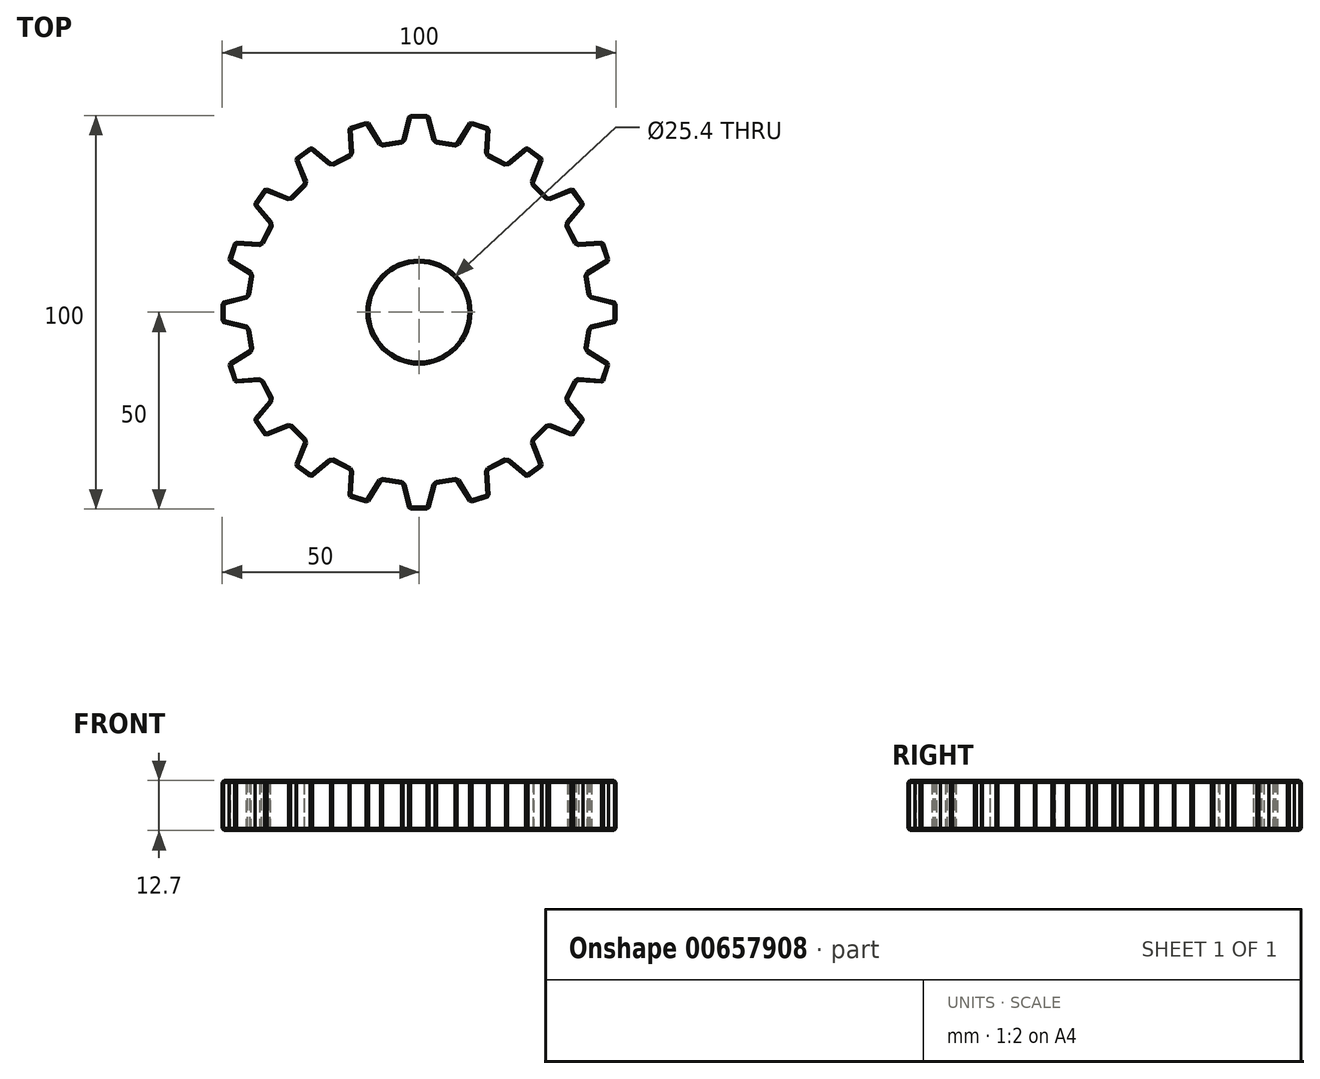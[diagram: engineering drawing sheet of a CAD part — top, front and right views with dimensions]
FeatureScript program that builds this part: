
annotation { "Feature Type Name" : "Feature", "Feature Type Description" : "" }
export const myFeature = defineFeature(function(context is Context, id is Id, definition is map)
    precondition{}
    {
        {
            var Q0;
            Q0=qCreatedBy(makeId("Top.planeOp"),FACE);
            var sketch = newSketch(context, id + "F0", { "sketchPlane" : qUnion([Q0])});
            skLineSegment(sketch, "E0", {"start": v(2.5, 50) * mm, "end": v(4.11, 43.54) * mm});
            skLineSegment(sketch, "E1.MirrorCS", {"start": v(-2.5, 50) * mm, "end": v(-4.11, 43.54) * mm});
            skLineSegment(sketch, "E2", {"start": v(4.11, 43.54) * mm, "end": v(9.54, 42.68) * mm});
            skLineSegment(sketch, "E3", {"start": v(-2.5, 50) * mm, "end": v(2.5, 50) * mm});
            skLineSegment(sketch, "E4", {"start": v(6.83, 43.1) * mm, "end": v(7.6, 48.05) * mm, "construction": true});
            skLineSegment(sketch, "E5.1.0", {"start": v(-17.83, 46.78) * mm, "end": v(-17.36, 40.14) * mm});
            skLineSegment(sketch, "E5.1.1", {"start": v(-17.83, 46.78) * mm, "end": v(-13.07, 48.33) * mm});
            skLineSegment(sketch, "E5.1.2", {"start": v(-13.07, 48.33) * mm, "end": v(-9.54, 42.68) * mm});
            skLineSegment(sketch, "E5.1.3", {"start": v(-9.54, 42.68) * mm, "end": v(-4.11, 43.54) * mm});
            skLineSegment(sketch, "E5.2.0", {"start": v(-31.41, 38.98) * mm, "end": v(-28.92, 32.8) * mm});
            skLineSegment(sketch, "E5.2.1", {"start": v(-31.41, 38.98) * mm, "end": v(-27.37, 41.92) * mm});
            skLineSegment(sketch, "E5.2.2", {"start": v(-27.37, 41.92) * mm, "end": v(-22.26, 37.64) * mm});
            skLineSegment(sketch, "E5.2.3", {"start": v(-22.26, 37.64) * mm, "end": v(-17.36, 40.14) * mm});
            skPoint(sketch, "E5.center", {"position": v(0, 0) * mm});
            skLineSegment(sketch, "E6.2.3.0", {"start": v(-41.92, 27.37) * mm, "end": v(-37.64, 22.26) * mm});
            skLineSegment(sketch, "E6.3.3.0", {"start": v(-41.92, 27.37) * mm, "end": v(-38.98, 31.41) * mm});
            skLineSegment(sketch, "E6.6.3.0", {"start": v(-38.98, 31.41) * mm, "end": v(-32.8, 28.92) * mm});
            skLineSegment(sketch, "E6.9.3.0", {"start": v(-32.8, 28.92) * mm, "end": v(-28.92, 32.8) * mm});
            skLineSegment(sketch, "E6.2.4.0", {"start": v(-48.33, 13.07) * mm, "end": v(-42.68, 9.54) * mm});
            skLineSegment(sketch, "E6.3.4.0", {"start": v(-48.33, 13.07) * mm, "end": v(-46.78, 17.83) * mm});
            skLineSegment(sketch, "E6.6.4.0", {"start": v(-46.78, 17.83) * mm, "end": v(-40.14, 17.36) * mm});
            skLineSegment(sketch, "E6.9.4.0", {"start": v(-40.14, 17.36) * mm, "end": v(-37.64, 22.26) * mm});
            skLineSegment(sketch, "E6.2.5.0", {"start": v(-50, -2.5) * mm, "end": v(-43.54, -4.11) * mm});
            skLineSegment(sketch, "E6.3.5.0", {"start": v(-50, -2.5) * mm, "end": v(-50, 2.5) * mm});
            skLineSegment(sketch, "E6.6.5.0", {"start": v(-50, 2.5) * mm, "end": v(-43.54, 4.11) * mm});
            skLineSegment(sketch, "E6.9.5.0", {"start": v(-43.54, 4.11) * mm, "end": v(-42.68, 9.54) * mm});
            skLineSegment(sketch, "E6.2.6.0", {"start": v(-46.78, -17.83) * mm, "end": v(-40.14, -17.36) * mm});
            skLineSegment(sketch, "E6.3.6.0", {"start": v(-46.78, -17.83) * mm, "end": v(-48.33, -13.07) * mm});
            skLineSegment(sketch, "E6.6.6.0", {"start": v(-48.33, -13.07) * mm, "end": v(-42.68, -9.54) * mm});
            skLineSegment(sketch, "E6.9.6.0", {"start": v(-42.68, -9.54) * mm, "end": v(-43.54, -4.11) * mm});
            skLineSegment(sketch, "E6.2.7.0", {"start": v(-38.98, -31.41) * mm, "end": v(-32.8, -28.92) * mm});
            skLineSegment(sketch, "E6.3.7.0", {"start": v(-38.98, -31.41) * mm, "end": v(-41.92, -27.37) * mm});
            skLineSegment(sketch, "E6.6.7.0", {"start": v(-41.92, -27.37) * mm, "end": v(-37.64, -22.26) * mm});
            skLineSegment(sketch, "E6.9.7.0", {"start": v(-37.64, -22.26) * mm, "end": v(-40.14, -17.36) * mm});
            skLineSegment(sketch, "E6.2.8.0", {"start": v(-27.37, -41.92) * mm, "end": v(-22.26, -37.64) * mm});
            skLineSegment(sketch, "E6.3.8.0", {"start": v(-27.37, -41.92) * mm, "end": v(-31.41, -38.98) * mm});
            skLineSegment(sketch, "E6.6.8.0", {"start": v(-31.41, -38.98) * mm, "end": v(-28.92, -32.8) * mm});
            skLineSegment(sketch, "E6.9.8.0", {"start": v(-28.92, -32.8) * mm, "end": v(-32.8, -28.92) * mm});
            skLineSegment(sketch, "E6.2.9.0", {"start": v(-13.07, -48.33) * mm, "end": v(-9.54, -42.68) * mm});
            skLineSegment(sketch, "E6.3.9.0", {"start": v(-13.07, -48.33) * mm, "end": v(-17.83, -46.78) * mm});
            skLineSegment(sketch, "E6.6.9.0", {"start": v(-17.83, -46.78) * mm, "end": v(-17.36, -40.14) * mm});
            skLineSegment(sketch, "E6.9.9.0", {"start": v(-17.36, -40.14) * mm, "end": v(-22.26, -37.64) * mm});
            skLineSegment(sketch, "E6.2.10.0", {"start": v(2.5, -50) * mm, "end": v(4.11, -43.54) * mm});
            skLineSegment(sketch, "E6.3.10.0", {"start": v(2.5, -50) * mm, "end": v(-2.5, -50) * mm});
            skLineSegment(sketch, "E6.6.10.0", {"start": v(-2.5, -50) * mm, "end": v(-4.11, -43.54) * mm});
            skLineSegment(sketch, "E6.9.10.0", {"start": v(-4.11, -43.54) * mm, "end": v(-9.54, -42.68) * mm});
            skLineSegment(sketch, "E6.2.11.0", {"start": v(17.83, -46.78) * mm, "end": v(17.36, -40.14) * mm});
            skLineSegment(sketch, "E6.3.11.0", {"start": v(17.83, -46.78) * mm, "end": v(13.07, -48.33) * mm});
            skLineSegment(sketch, "E6.6.11.0", {"start": v(13.07, -48.33) * mm, "end": v(9.54, -42.68) * mm});
            skLineSegment(sketch, "E6.9.11.0", {"start": v(9.54, -42.68) * mm, "end": v(4.11, -43.54) * mm});
            skLineSegment(sketch, "E6.2.12.0", {"start": v(31.41, -38.98) * mm, "end": v(28.92, -32.8) * mm});
            skLineSegment(sketch, "E6.3.12.0", {"start": v(31.41, -38.98) * mm, "end": v(27.37, -41.92) * mm});
            skLineSegment(sketch, "E6.6.12.0", {"start": v(27.37, -41.92) * mm, "end": v(22.26, -37.64) * mm});
            skLineSegment(sketch, "E6.9.12.0", {"start": v(22.26, -37.64) * mm, "end": v(17.36, -40.14) * mm});
            skLineSegment(sketch, "E6.2.13.0", {"start": v(41.92, -27.37) * mm, "end": v(37.64, -22.26) * mm});
            skLineSegment(sketch, "E6.3.13.0", {"start": v(41.92, -27.37) * mm, "end": v(38.98, -31.41) * mm});
            skLineSegment(sketch, "E6.6.13.0", {"start": v(38.98, -31.41) * mm, "end": v(32.8, -28.92) * mm});
            skLineSegment(sketch, "E6.9.13.0", {"start": v(32.8, -28.92) * mm, "end": v(28.92, -32.8) * mm});
            skLineSegment(sketch, "E6.2.14.0", {"start": v(48.33, -13.07) * mm, "end": v(42.68, -9.54) * mm});
            skLineSegment(sketch, "E6.3.14.0", {"start": v(48.33, -13.07) * mm, "end": v(46.78, -17.83) * mm});
            skLineSegment(sketch, "E6.6.14.0", {"start": v(46.78, -17.83) * mm, "end": v(40.14, -17.36) * mm});
            skLineSegment(sketch, "E6.9.14.0", {"start": v(40.14, -17.36) * mm, "end": v(37.64, -22.26) * mm});
            skLineSegment(sketch, "E6.2.15.0", {"start": v(50, 2.5) * mm, "end": v(43.54, 4.11) * mm});
            skLineSegment(sketch, "E6.3.15.0", {"start": v(50, 2.5) * mm, "end": v(50, -2.5) * mm});
            skLineSegment(sketch, "E6.6.15.0", {"start": v(50, -2.5) * mm, "end": v(43.54, -4.11) * mm});
            skLineSegment(sketch, "E6.9.15.0", {"start": v(43.54, -4.11) * mm, "end": v(42.68, -9.54) * mm});
            skLineSegment(sketch, "E6.2.16.0", {"start": v(46.78, 17.83) * mm, "end": v(40.14, 17.36) * mm});
            skLineSegment(sketch, "E6.3.16.0", {"start": v(46.78, 17.83) * mm, "end": v(48.33, 13.07) * mm});
            skLineSegment(sketch, "E6.6.16.0", {"start": v(48.33, 13.07) * mm, "end": v(42.68, 9.54) * mm});
            skLineSegment(sketch, "E6.9.16.0", {"start": v(42.68, 9.54) * mm, "end": v(43.54, 4.11) * mm});
            skLineSegment(sketch, "E6.2.17.0", {"start": v(38.98, 31.41) * mm, "end": v(32.8, 28.92) * mm});
            skLineSegment(sketch, "E6.3.17.0", {"start": v(38.98, 31.41) * mm, "end": v(41.92, 27.37) * mm});
            skLineSegment(sketch, "E6.6.17.0", {"start": v(41.92, 27.37) * mm, "end": v(37.64, 22.26) * mm});
            skLineSegment(sketch, "E6.9.17.0", {"start": v(37.64, 22.26) * mm, "end": v(40.14, 17.36) * mm});
            skLineSegment(sketch, "E6.2.18.0", {"start": v(27.37, 41.92) * mm, "end": v(22.26, 37.64) * mm});
            skLineSegment(sketch, "E6.3.18.0", {"start": v(27.37, 41.92) * mm, "end": v(31.41, 38.98) * mm});
            skLineSegment(sketch, "E6.6.18.0", {"start": v(31.41, 38.98) * mm, "end": v(28.92, 32.8) * mm});
            skLineSegment(sketch, "E6.9.18.0", {"start": v(28.92, 32.8) * mm, "end": v(32.8, 28.92) * mm});
            skLineSegment(sketch, "E6.2.19.0", {"start": v(13.07, 48.33) * mm, "end": v(9.54, 42.68) * mm});
            skLineSegment(sketch, "E6.3.19.0", {"start": v(13.07, 48.33) * mm, "end": v(17.83, 46.78) * mm});
            skLineSegment(sketch, "E6.6.19.0", {"start": v(17.83, 46.78) * mm, "end": v(17.36, 40.14) * mm});
            skLineSegment(sketch, "E6.9.19.0", {"start": v(17.36, 40.14) * mm, "end": v(22.26, 37.64) * mm});
            skLineSegment(sketch, "E7", {"start": v(0, 50) * mm, "end": v(0, 0) * mm, "construction": true});
            skLineSegment(sketch, "E8", {"start": v(-4.11, 43.54) * mm, "end": v(4.11, 43.54) * mm, "construction": true});
            skCircle(sketch, "E9", {"center": v(0, 0) * mm, "radius": 12.7 * mm});
            skSolve(sketch);
        }
        {
            var Q0;
            Q0=makeQuery(id+"F0.imprint","IMPRINT",FACE,{"disambiguationData":[TD([[makeQuery(id+"F0.imprint","IMPRINT",EDGE,{"derivedFrom":sQuery(id+"F0.wireOp",EDGE,"E0")}),-1.0]])]});
            var Q1;
            Q1=sQuery(id+"F0.wireOp",EDGE,"E6.3.6.0");
            var Q2;
            Q2=sQuery(id+"F0.wireOp",EDGE,"E6.9.6.0");
            var Q3;
            Q3=sQuery(id+"F0.wireOp",EDGE,"E6.2.5.0");
            var Q4;
            Q4=sQuery(id+"F0.wireOp",EDGE,"E6.3.5.0");
            var Q5;
            Q5=sQuery(id+"F0.wireOp",EDGE,"E6.6.5.0");
            var Q6;
            Q6=sQuery(id+"F0.wireOp",EDGE,"E6.9.5.0");
            var Q7;
            Q7=sQuery(id+"F0.wireOp",EDGE,"E6.2.4.0");
            var Q8;
            Q8=sQuery(id+"F0.wireOp",EDGE,"E6.3.4.0");
            var Q9;
            Q9=sQuery(id+"F0.wireOp",EDGE,"E6.6.4.0");
            var Q10;
            Q10=sQuery(id+"F0.wireOp",EDGE,"E6.9.4.0");
            var Q11;
            Q11=sQuery(id+"F0.wireOp",EDGE,"E6.2.3.0");
            var Q12;
            Q12=sQuery(id+"F0.wireOp",EDGE,"E6.3.3.0");
            var Q13;
            Q13=sQuery(id+"F0.wireOp",EDGE,"E6.6.3.0");
            var Q14;
            Q14=sQuery(id+"F0.wireOp",EDGE,"E5.2.0");
            var Q15;
            Q15=sQuery(id+"F0.wireOp",EDGE,"E6.9.3.0");
            var Q16;
            Q16=sQuery(id+"F0.wireOp",EDGE,"E6.6.6.0");
            extrude(context, id + "F1", {"entities" : qUnion([Q0]), "surfaceEntities" : qUnion([Q1, Q2, Q3, Q4, Q5, Q6, Q7, Q8, Q9, Q10, Q11, Q12, Q13, Q14, Q15, Q16]), "endBound" : BoundingType.SYMMETRIC, "depth" : 12.7 * mm, "offsetDistance" : 25 * mm, "hasSecondDirectionDraft" : true, "secondDirectionDraftAngle" : 5 * degree});
        }
        {
            var Q0;
            Q0=makeQuery(id+"F1.opExtrude","SWEPT_FACE",FACE,{"disambiguationData":[OSD([sQuery(id+"F0.wireOp",EDGE,"E5.2.0")])]});
            var Q1;
            Q1=makeQuery(id+"F1.opExtrude","CAP_EDGE",EDGE,{"disambiguationData":[OSD([sQuery(id+"F0.wireOp",EDGE,"E6.3.17.0")])],"isStart":true});
            var Q2;
            Q2=makeQuery(id+"F1.opExtrude","CAP_EDGE",EDGE,{"disambiguationData":[OSD([sQuery(id+"F0.wireOp",EDGE,"E6.6.11.0")])],"isStart":true});
            var Q3;
            Q3=makeQuery(id+"F1.opExtrude","CAP_EDGE",EDGE,{"disambiguationData":[OSD([sQuery(id+"F0.wireOp",EDGE,"E9")])],"isStart":false});
            var Q4;
            Q4=makeQuery(id+"F1.opExtrude","SWEPT_FACE",FACE,{"disambiguationData":[OSD([sQuery(id+"F0.wireOp",EDGE,"E6.2.17.0")])]});
            var Q5;
            Q5=makeQuery(id+"F1.opExtrude","SWEPT_FACE",FACE,{"disambiguationData":[OSD([sQuery(id+"F0.wireOp",EDGE,"E6.9.12.0")])]});
            var Q6;
            Q6=makeQuery(id+"F1.opExtrude","SWEPT_FACE",FACE,{"disambiguationData":[OSD([sQuery(id+"F0.wireOp",EDGE,"E6.6.13.0")])]});
            var Q7;
            Q7=makeQuery(id+"F1.opExtrude","CAP_EDGE",EDGE,{"disambiguationData":[OSD([sQuery(id+"F0.wireOp",EDGE,"E6.6.10.0")])],"isStart":true});
            var Q8;
            Q8=makeQuery(id+"F1.opExtrude","SWEPT_EDGE",EDGE,{"disambiguationData":[OSD([sQuery(id+"F0.wireOp",EDGE,"E6.6.5.0"),sQuery(id+"F0.wireOp",EDGE,"E6.9.5.0")])]});
            var Q9;
            Q9=makeQuery(id+"F1.opExtrude","SWEPT_FACE",FACE,{"disambiguationData":[OSD([sQuery(id+"F0.wireOp",EDGE,"E6.6.8.0")])]});
            var Q10;
            Q10=makeQuery(id+"F1.opExtrude","SWEPT_FACE",FACE,{"disambiguationData":[OSD([sQuery(id+"F0.wireOp",EDGE,"E6.6.5.0")])]});
            var Q11;
            Q11=makeQuery(id+"F1.opExtrude","SWEPT_FACE",FACE,{"disambiguationData":[OSD([sQuery(id+"F0.wireOp",EDGE,"E5.2.1")])]});
            var Q12;
            Q12=makeQuery(id+"F1.opExtrude","SWEPT_FACE",FACE,{"disambiguationData":[OSD([sQuery(id+"F0.wireOp",EDGE,"E6.9.6.0")])]});
            var Q13;
            Q13=makeQuery(id+"F1.opExtrude","SWEPT_FACE",FACE,{"disambiguationData":[OSD([sQuery(id+"F0.wireOp",EDGE,"E6.6.17.0")])]});
            var Q14;
            Q14=makeQuery(id+"F1.opExtrude","CAP_EDGE",EDGE,{"disambiguationData":[OSD([sQuery(id+"F0.wireOp",EDGE,"E6.3.7.0")])],"isStart":false});
            var Q15;
            Q15=makeQuery(id+"F1.opExtrude","CAP_EDGE",EDGE,{"disambiguationData":[OSD([sQuery(id+"F0.wireOp",EDGE,"E6.2.12.0")])],"isStart":false});
            var Q16;
            Q16=makeQuery(id+"F1.opExtrude","CAP_EDGE",EDGE,{"disambiguationData":[OSD([sQuery(id+"F0.wireOp",EDGE,"E6.9.5.0")])],"isStart":true});
            var Q17;
            Q17=makeQuery(id+"F1.opExtrude","SWEPT_FACE",FACE,{"disambiguationData":[OSD([sQuery(id+"F0.wireOp",EDGE,"E6.6.11.0")])]});
            var Q18;
            Q18=makeQuery(id+"F1.opExtrude","SWEPT_FACE",FACE,{"disambiguationData":[OSD([sQuery(id+"F0.wireOp",EDGE,"E6.6.16.0")])]});
            var Q19;
            Q19=makeQuery(id+"F1.opExtrude","SWEPT_FACE",FACE,{"disambiguationData":[OSD([sQuery(id+"F0.wireOp",EDGE,"E6.3.16.0")])]});
            var Q20;
            Q20=makeQuery(id+"F1.opExtrude","CAP_EDGE",EDGE,{"disambiguationData":[OSD([sQuery(id+"F0.wireOp",EDGE,"E6.9.7.0")])],"isStart":true});
            var Q21;
            Q21=makeQuery(id+"F1.opExtrude","SWEPT_EDGE",EDGE,{"disambiguationData":[OSD([sQuery(id+"F0.wireOp",EDGE,"E6.6.12.0"),sQuery(id+"F0.wireOp",EDGE,"E6.9.12.0")])]});
            var Q22;
            Q22=makeQuery(id+"F1.opExtrude","SWEPT_EDGE",EDGE,{"disambiguationData":[OSD([sQuery(id+"F0.wireOp",EDGE,"E6.2.7.0"),sQuery(id+"F0.wireOp",EDGE,"E6.9.8.0")])]});
            var Q23;
            Q23=makeQuery(id+"F1.opExtrude","CAP_EDGE",EDGE,{"disambiguationData":[OSD([sQuery(id+"F0.wireOp",EDGE,"E6.9.9.0")])],"isStart":true});
            var Q24;
            Q24=makeQuery(id+"F1.opExtrude","SWEPT_FACE",FACE,{"disambiguationData":[OSD([sQuery(id+"F0.wireOp",EDGE,"E6.3.10.0")])]});
            var Q25;
            Q25=makeQuery(id+"F1.opExtrude","SWEPT_FACE",FACE,{"disambiguationData":[OSD([sQuery(id+"F0.wireOp",EDGE,"E6.3.4.0")])]});
            var Q26;
            Q26=makeQuery(id+"F1.opExtrude","SWEPT_FACE",FACE,{"disambiguationData":[OSD([sQuery(id+"F0.wireOp",EDGE,"E6.2.13.0")])]});
            var Q27;
            Q27=makeQuery(id+"F1.opExtrude","SWEPT_EDGE",EDGE,{"disambiguationData":[OSD([sQuery(id+"F0.wireOp",EDGE,"E6.2.13.0"),sQuery(id+"F0.wireOp",EDGE,"E6.3.13.0")])]});
            var Q28;
            Q28=makeQuery(id+"F1.opExtrude","SWEPT_FACE",FACE,{"disambiguationData":[OSD([sQuery(id+"F0.wireOp",EDGE,"E6.9.3.0")])]});
            var Q29;
            Q29=makeQuery(id+"F1.opExtrude","SWEPT_FACE",FACE,{"disambiguationData":[OSD([sQuery(id+"F0.wireOp",EDGE,"E6.3.19.0")])]});
            var Q30;
            Q30=makeQuery(id+"F1.opExtrude","SWEPT_FACE",FACE,{"disambiguationData":[OSD([sQuery(id+"F0.wireOp",EDGE,"E6.9.8.0")])]});
            var Q31;
            Q31=makeQuery(id+"F1.opExtrude","SWEPT_FACE",FACE,{"disambiguationData":[OSD([sQuery(id+"F0.wireOp",EDGE,"E6.2.15.0")])]});
            var Q32;
            Q32=makeQuery(id+"F1.opExtrude","CAP_EDGE",EDGE,{"disambiguationData":[OSD([sQuery(id+"F0.wireOp",EDGE,"E6.6.18.0")])],"isStart":false});
            var Q33;
            Q33=makeQuery(id+"F1.opExtrude","SWEPT_FACE",FACE,{"disambiguationData":[OSD([sQuery(id+"F0.wireOp",EDGE,"E6.3.9.0")])]});
            var Q34;
            Q34=makeQuery(id+"F1.opExtrude","SWEPT_EDGE",EDGE,{"disambiguationData":[OSD([sQuery(id+"F0.wireOp",EDGE,"E6.3.15.0"),sQuery(id+"F0.wireOp",EDGE,"E6.6.15.0")])]});
            var Q35;
            Q35=makeQuery(id+"F1.opExtrude","SWEPT_FACE",FACE,{"disambiguationData":[OSD([sQuery(id+"F0.wireOp",EDGE,"E3")])]});
            var Q36;
            Q36=makeQuery(id+"F1.opExtrude","SWEPT_FACE",FACE,{"disambiguationData":[OSD([sQuery(id+"F0.wireOp",EDGE,"E5.1.2")])]});
            var Q37;
            Q37=makeQuery(id+"F1.opExtrude","SWEPT_EDGE",EDGE,{"disambiguationData":[OSD([sQuery(id+"F0.wireOp",EDGE,"E6.6.15.0"),sQuery(id+"F0.wireOp",EDGE,"E6.9.15.0")])]});
            var Q38;
            Q38=makeQuery(id+"F1.opExtrude","SWEPT_FACE",FACE,{"disambiguationData":[OSD([sQuery(id+"F0.wireOp",EDGE,"E5.1.0")])]});
            var Q39;
            Q39=makeQuery(id+"F1.opExtrude","SWEPT_FACE",FACE,{"disambiguationData":[OSD([sQuery(id+"F0.wireOp",EDGE,"E6.9.16.0")])]});
            var Q40;
            Q40=makeQuery(id+"F1.opExtrude","SWEPT_FACE",FACE,{"disambiguationData":[OSD([sQuery(id+"F0.wireOp",EDGE,"E6.2.9.0")])]});
            var Q41;
            Q41=makeQuery(id+"F1.opExtrude","SWEPT_EDGE",EDGE,{"disambiguationData":[OSD([sQuery(id+"F0.wireOp",EDGE,"E6.3.3.0"),sQuery(id+"F0.wireOp",EDGE,"E6.6.3.0")])]});
            var Q42;
            Q42=makeQuery(id+"F1.opExtrude","SWEPT_EDGE",EDGE,{"disambiguationData":[OSD([sQuery(id+"F0.wireOp",EDGE,"E6.2.12.0"),sQuery(id+"F0.wireOp",EDGE,"E6.3.12.0")])]});
            var Q43;
            Q43=makeQuery(id+"F1.opExtrude","SWEPT_FACE",FACE,{"disambiguationData":[OSD([sQuery(id+"F0.wireOp",EDGE,"E6.2.4.0")])]});
            var Q44;
            Q44=makeQuery(id+"F1.opExtrude","SWEPT_EDGE",EDGE,{"disambiguationData":[OSD([sQuery(id+"F0.wireOp",EDGE,"E6.2.5.0"),sQuery(id+"F0.wireOp",EDGE,"E6.9.6.0")])]});
            var Q45;
            Q45=makeQuery(id+"F1.opExtrude","SWEPT_FACE",FACE,{"disambiguationData":[OSD([sQuery(id+"F0.wireOp",EDGE,"E6.9.11.0")])]});
            var Q46;
            Q46=makeQuery(id+"F1.opExtrude","SWEPT_FACE",FACE,{"disambiguationData":[OSD([sQuery(id+"F0.wireOp",EDGE,"E6.2.7.0")])]});
            var Q47;
            Q47=makeQuery(id+"F1.opExtrude","SWEPT_EDGE",EDGE,{"disambiguationData":[OSD([sQuery(id+"F0.wireOp",EDGE,"E6.2.13.0"),sQuery(id+"F0.wireOp",EDGE,"E6.9.14.0")])]});
            var Q48;
            Q48=makeQuery(id+"F1.opExtrude","SWEPT_FACE",FACE,{"disambiguationData":[OSD([sQuery(id+"F0.wireOp",EDGE,"E6.3.17.0")])]});
            var Q49;
            Q49=makeQuery(id+"F1.opExtrude","SWEPT_FACE",FACE,{"disambiguationData":[OSD([sQuery(id+"F0.wireOp",EDGE,"E6.2.5.0")])]});
            var Q50;
            Q50=makeQuery(id+"F1.opExtrude","CAP_EDGE",EDGE,{"disambiguationData":[OSD([sQuery(id+"F0.wireOp",EDGE,"E6.9.13.0")])],"isStart":true});
            var Q51;
            Q51=makeQuery(id+"F1.opExtrude","CAP_EDGE",EDGE,{"disambiguationData":[OSD([sQuery(id+"F0.wireOp",EDGE,"E6.3.15.0")])],"isStart":true});
            var Q52;
            Q52=makeQuery(id+"F1.opExtrude","CAP_EDGE",EDGE,{"disambiguationData":[OSD([sQuery(id+"F0.wireOp",EDGE,"E6.6.3.0")])],"isStart":false});
            var Q53;
            Q53=makeQuery(id+"F1.opExtrude","SWEPT_FACE",FACE,{"disambiguationData":[OSD([sQuery(id+"F0.wireOp",EDGE,"E5.1.1")])]});
            var Q54;
            Q54=makeQuery(id+"F1.opExtrude","CAP_EDGE",EDGE,{"disambiguationData":[OSD([sQuery(id+"F0.wireOp",EDGE,"E6.2.10.0")])],"isStart":false});
            var Q55;
            Q55=makeQuery(id+"F1.opExtrude","SWEPT_FACE",FACE,{"disambiguationData":[OSD([sQuery(id+"F0.wireOp",EDGE,"E6.3.8.0")])]});
            var Q56;
            Q56=makeQuery(id+"F1.opExtrude","SWEPT_FACE",FACE,{"disambiguationData":[OSD([sQuery(id+"F0.wireOp",EDGE,"E6.9.9.0")])]});
            var Q57;
            Q57=makeQuery(id+"F1.opExtrude","SWEPT_FACE",FACE,{"disambiguationData":[OSD([sQuery(id+"F0.wireOp",EDGE,"E6.6.18.0")])]});
            var Q58;
            Q58=makeQuery(id+"F1.opExtrude","SWEPT_FACE",FACE,{"disambiguationData":[OSD([sQuery(id+"F0.wireOp",EDGE,"E6.6.6.0")])]});
            var Q59;
            Q59=makeQuery(id+"F1.opExtrude","SWEPT_FACE",FACE,{"disambiguationData":[OSD([sQuery(id+"F0.wireOp",EDGE,"E6.9.13.0")])]});
            var Q60;
            Q60=makeQuery(id+"F1.opExtrude","SWEPT_EDGE",EDGE,{"disambiguationData":[OSD([sQuery(id+"F0.wireOp",EDGE,"E5.1.0"),sQuery(id+"F0.wireOp",EDGE,"E5.1.1")])]});
            var Q61;
            Q61=makeQuery(id+"F1.opExtrude","CAP_EDGE",EDGE,{"disambiguationData":[OSD([sQuery(id+"F0.wireOp",EDGE,"E6.9.17.0")])],"isStart":false});
            var Q62;
            Q62=makeQuery(id+"F1.opExtrude","SWEPT_FACE",FACE,{"disambiguationData":[OSD([sQuery(id+"F0.wireOp",EDGE,"E5.1.3")])]});
            var Q63;
            Q63=makeQuery(id+"F1.opExtrude","SWEPT_EDGE",EDGE,{"disambiguationData":[OSD([sQuery(id+"F0.wireOp",EDGE,"E6.2.15.0"),sQuery(id+"F0.wireOp",EDGE,"E6.3.15.0")])]});
            var Q64;
            Q64=makeQuery(id+"F1.opExtrude","SWEPT_FACE",FACE,{"disambiguationData":[OSD([sQuery(id+"F0.wireOp",EDGE,"E5.2.3")])]});
            var Q65;
            Q65=makeQuery(id+"F1.opExtrude","CAP_EDGE",EDGE,{"disambiguationData":[OSD([sQuery(id+"F0.wireOp",EDGE,"E6.3.18.0")])],"isStart":false});
            var Q66;
            Q66=makeQuery(id+"F1.opExtrude","SWEPT_FACE",FACE,{"disambiguationData":[OSD([sQuery(id+"F0.wireOp",EDGE,"E5.2.2")])]});
            var Q67;
            Q67=makeQuery(id+"F1.opExtrude","CAP_EDGE",EDGE,{"disambiguationData":[OSD([sQuery(id+"F0.wireOp",EDGE,"E6.2.14.0")])],"isStart":false});
            var Q68;
            Q68=makeQuery(id+"F1.opExtrude","SWEPT_FACE",FACE,{"disambiguationData":[OSD([sQuery(id+"F0.wireOp",EDGE,"E6.6.9.0")])]});
            var Q69;
            Q69=makeQuery(id+"F1.opExtrude","SWEPT_FACE",FACE,{"disambiguationData":[OSD([sQuery(id+"F0.wireOp",EDGE,"E6.9.10.0")])]});
            var Q70;
            Q70=makeQuery(id+"F1.opExtrude","SWEPT_FACE",FACE,{"disambiguationData":[OSD([sQuery(id+"F0.wireOp",EDGE,"E6.3.6.0")])]});
            var Q71;
            Q71=makeQuery(id+"F1.opExtrude","CAP_EDGE",EDGE,{"disambiguationData":[OSD([sQuery(id+"F0.wireOp",EDGE,"E6.2.18.0")])],"isStart":true});
            var Q72;
            Q72=makeQuery(id+"F1.opExtrude","CAP_EDGE",EDGE,{"disambiguationData":[OSD([sQuery(id+"F0.wireOp",EDGE,"E5.2.0")])],"isStart":true});
            var Q73;
            Q73=makeQuery(id+"F1.opExtrude","SWEPT_FACE",FACE,{"disambiguationData":[OSD([sQuery(id+"F0.wireOp",EDGE,"E6.9.5.0")])]});
            var Q74;
            Q74=makeQuery(id+"F1.opExtrude","SWEPT_FACE",FACE,{"disambiguationData":[OSD([sQuery(id+"F0.wireOp",EDGE,"E6.2.3.0")])]});
            var Q75;
            Q75=makeQuery(id+"F1.opExtrude","SWEPT_EDGE",EDGE,{"disambiguationData":[OSD([sQuery(id+"F0.wireOp",EDGE,"E6.3.7.0"),sQuery(id+"F0.wireOp",EDGE,"E6.6.7.0")])]});
            var Q76;
            Q76=makeQuery(id+"F1.opExtrude","SWEPT_FACE",FACE,{"disambiguationData":[OSD([sQuery(id+"F0.wireOp",EDGE,"E6.9.19.0")])]});
            var Q77;
            Q77=makeQuery(id+"F1.opExtrude","SWEPT_FACE",FACE,{"disambiguationData":[OSD([sQuery(id+"F0.wireOp",EDGE,"E6.3.13.0")])]});
            var Q78;
            Q78=makeQuery(id+"F1.opExtrude","SWEPT_FACE",FACE,{"disambiguationData":[OSD([sQuery(id+"F0.wireOp",EDGE,"E6.6.15.0")])]});
            var Q79;
            Q79=makeQuery(id+"F1.opExtrude","CAP_EDGE",EDGE,{"disambiguationData":[OSD([sQuery(id+"F0.wireOp",EDGE,"E6.3.6.0")])],"isStart":true});
            var Q80;
            Q80=makeQuery(id+"F1.opExtrude","SWEPT_FACE",FACE,{"disambiguationData":[OSD([sQuery(id+"F0.wireOp",EDGE,"E6.9.18.0")])]});
            var Q81;
            Q81=makeQuery(id+"F1.opExtrude","SWEPT_FACE",FACE,{"disambiguationData":[OSD([sQuery(id+"F0.wireOp",EDGE,"E6.6.10.0")])]});
            var Q82;
            Q82=makeQuery(id+"F1.opExtrude","CAP_EDGE",EDGE,{"disambiguationData":[OSD([sQuery(id+"F0.wireOp",EDGE,"E6.6.19.0")])],"isStart":false});
            var Q83;
            Q83=makeQuery(id+"F1.opExtrude","SWEPT_FACE",FACE,{"disambiguationData":[OSD([sQuery(id+"F0.wireOp",EDGE,"E6.2.16.0")])]});
            var Q84;
            Q84=makeQuery(id+"F1.opExtrude","SWEPT_EDGE",EDGE,{"disambiguationData":[OSD([sQuery(id+"F0.wireOp",EDGE,"E6.2.17.0"),sQuery(id+"F0.wireOp",EDGE,"E6.9.18.0")])]});
            var Q85;
            Q85=makeQuery(id+"F1.opExtrude","CAP_EDGE",EDGE,{"disambiguationData":[OSD([sQuery(id+"F0.wireOp",EDGE,"E6.3.12.0")])],"isStart":true});
            var Q86;
            Q86=makeQuery(id+"F1.opExtrude","SWEPT_FACE",FACE,{"disambiguationData":[OSD([sQuery(id+"F0.wireOp",EDGE,"E6.6.7.0")])]});
            var Q87;
            Q87=makeQuery(id+"F1.opExtrude","SWEPT_EDGE",EDGE,{"disambiguationData":[OSD([sQuery(id+"F0.wireOp",EDGE,"E5.2.0"),sQuery(id+"F0.wireOp",EDGE,"E5.2.1")])]});
            var Q88;
            Q88=makeQuery(id+"F1.opExtrude","SWEPT_FACE",FACE,{"disambiguationData":[OSD([sQuery(id+"F0.wireOp",EDGE,"E6.3.5.0")])]});
            var Q89;
            Q89=makeQuery(id+"F1.opExtrude","SWEPT_FACE",FACE,{"disambiguationData":[OSD([sQuery(id+"F0.wireOp",EDGE,"E6.2.10.0")])]});
            var Q90;
            Q90=makeQuery(id+"F1.opExtrude","CAP_EDGE",EDGE,{"disambiguationData":[OSD([sQuery(id+"F0.wireOp",EDGE,"E6.6.16.0")])],"isStart":true});
            var Q91;
            Q91=makeQuery(id+"F1.opExtrude","SWEPT_FACE",FACE,{"disambiguationData":[OSD([sQuery(id+"F0.wireOp",EDGE,"E6.3.7.0")])]});
            var Q92;
            Q92=makeQuery(id+"F1.opExtrude","SWEPT_FACE",FACE,{"disambiguationData":[OSD([sQuery(id+"F0.wireOp",EDGE,"E6.2.12.0")])]});
            var Q93;
            Q93=makeQuery(id+"F1.opExtrude","SWEPT_FACE",FACE,{"disambiguationData":[OSD([sQuery(id+"F0.wireOp",EDGE,"E6.2.6.0")])]});
            var Q94;
            Q94=makeQuery(id+"F1.opExtrude","SWEPT_FACE",FACE,{"disambiguationData":[OSD([sQuery(id+"F0.wireOp",EDGE,"E6.6.19.0")])]});
            var Q95;
            Q95=makeQuery(id+"F1.opExtrude","SWEPT_FACE",FACE,{"disambiguationData":[OSD([sQuery(id+"F0.wireOp",EDGE,"E6.3.14.0")])]});
            var Q96;
            Q96=makeQuery(id+"F1.opExtrude","SWEPT_EDGE",EDGE,{"disambiguationData":[OSD([sQuery(id+"F0.wireOp",EDGE,"E6.2.9.0"),sQuery(id+"F0.wireOp",EDGE,"E6.3.9.0")])]});
            var Q97;
            Q97=makeQuery(id+"F1.opExtrude","SWEPT_FACE",FACE,{"disambiguationData":[OSD([sQuery(id+"F0.wireOp",EDGE,"E6.9.4.0")])]});
            var Q98;
            Q98=makeQuery(id+"F1.opExtrude","CAP_EDGE",EDGE,{"disambiguationData":[OSD([sQuery(id+"F0.wireOp",EDGE,"E6.9.17.0")])],"isStart":true});
            var Q99;
            Q99=makeQuery(id+"F1.opExtrude","SWEPT_EDGE",EDGE,{"disambiguationData":[OSD([sQuery(id+"F0.wireOp",EDGE,"E6.6.16.0"),sQuery(id+"F0.wireOp",EDGE,"E6.9.16.0")])]});
            var Q100;
            Q100=makeQuery(id+"F1.opExtrude","CAP_EDGE",EDGE,{"disambiguationData":[OSD([sQuery(id+"F0.wireOp",EDGE,"E5.2.0")])],"isStart":false});
            var Q101;
            Q101=makeQuery(id+"F1.opExtrude","SWEPT_FACE",FACE,{"disambiguationData":[OSD([sQuery(id+"F0.wireOp",EDGE,"E6.2.14.0")])]});
            var Q102;
            Q102=makeQuery(id+"F1.opExtrude","SWEPT_FACE",FACE,{"disambiguationData":[OSD([sQuery(id+"F0.wireOp",EDGE,"E6.6.4.0")])]});
            var Q103;
            Q103=makeQuery(id+"F1.opExtrude","CAP_EDGE",EDGE,{"disambiguationData":[OSD([sQuery(id+"F0.wireOp",EDGE,"E6.3.14.0")])],"isStart":false});
            var Q104;
            Q104=makeQuery(id+"F1.opExtrude","CAP_EDGE",EDGE,{"disambiguationData":[OSD([sQuery(id+"F0.wireOp",EDGE,"E6.2.8.0")])],"isStart":true});
            var Q105;
            Q105=makeQuery(id+"F1.opExtrude","SWEPT_FACE",FACE,{"disambiguationData":[OSD([sQuery(id+"F0.wireOp",EDGE,"E6.2.18.0")])]});
            var Q106;
            Q106=makeQuery(id+"F1.opExtrude","SWEPT_FACE",FACE,{"disambiguationData":[OSD([sQuery(id+"F0.wireOp",EDGE,"E6.9.15.0")])]});
            var Q107;
            Q107=makeQuery(id+"F1.opExtrude","SWEPT_FACE",FACE,{"disambiguationData":[OSD([sQuery(id+"F0.wireOp",EDGE,"E6.9.7.0")])]});
            var Q108;
            Q108=makeQuery(id+"F1.opExtrude","SWEPT_FACE",FACE,{"disambiguationData":[OSD([sQuery(id+"F0.wireOp",EDGE,"E6.3.3.0")])]});
            var Q109;
            Q109=makeQuery(id+"F1.opExtrude","SWEPT_EDGE",EDGE,{"disambiguationData":[OSD([sQuery(id+"F0.wireOp",EDGE,"E6.2.18.0"),sQuery(id+"F0.wireOp",EDGE,"E6.9.19.0")])]});
            var Q110;
            Q110=makeQuery(id+"F1.opExtrude","SWEPT_FACE",FACE,{"disambiguationData":[OSD([sQuery(id+"F0.wireOp",EDGE,"E6.3.15.0")])]});
            var Q111;
            Q111=makeQuery(id+"F1.opExtrude","SWEPT_EDGE",EDGE,{"disambiguationData":[OSD([sQuery(id+"F0.wireOp",EDGE,"E6.3.5.0"),sQuery(id+"F0.wireOp",EDGE,"E6.6.5.0")])]});
            var Q112;
            Q112=makeQuery(id+"F1.opExtrude","SWEPT_FACE",FACE,{"disambiguationData":[OSD([sQuery(id+"F0.wireOp",EDGE,"E6.2.11.0")])]});
            var Q113;
            Q113=makeQuery(id+"F1.opExtrude","SWEPT_FACE",FACE,{"disambiguationData":[OSD([sQuery(id+"F0.wireOp",EDGE,"E6.6.12.0")])]});
            var Q114;
            Q114=makeQuery(id+"F1.opExtrude","CAP_EDGE",EDGE,{"disambiguationData":[OSD([sQuery(id+"F0.wireOp",EDGE,"E6.6.11.0")])],"isStart":false});
            var Q115;
            Q115=makeQuery(id+"F1.opExtrude","CAP_EDGE",EDGE,{"disambiguationData":[OSD([sQuery(id+"F0.wireOp",EDGE,"E6.2.18.0")])],"isStart":false});
            var Q116;
            Q116=makeQuery(id+"F1.opExtrude","CAP_EDGE",EDGE,{"disambiguationData":[OSD([sQuery(id+"F0.wireOp",EDGE,"E6.6.14.0")])],"isStart":true});
            var Q117;
            Q117=makeQuery(id+"F1.opExtrude","SWEPT_FACE",FACE,{"disambiguationData":[OSD([sQuery(id+"F0.wireOp",EDGE,"E6.9.14.0")])]});
            var Q118;
            Q118=makeQuery(id+"F1.opExtrude","CAP_EDGE",EDGE,{"disambiguationData":[OSD([sQuery(id+"F0.wireOp",EDGE,"E5.1.2")])],"isStart":false});
            var Q119;
            Q119=makeQuery(id+"F1.opExtrude","CAP_EDGE",EDGE,{"disambiguationData":[OSD([sQuery(id+"F0.wireOp",EDGE,"E6.9.18.0")])],"isStart":false});
            var Q120;
            Q120=makeQuery(id+"F1.opExtrude","SWEPT_FACE",FACE,{"disambiguationData":[OSD([sQuery(id+"F0.wireOp",EDGE,"E6.2.19.0")])]});
            var Q121;
            Q121=makeQuery(id+"F1.opExtrude","CAP_EDGE",EDGE,{"disambiguationData":[OSD([sQuery(id+"F0.wireOp",EDGE,"E6.2.11.0")])],"isStart":true});
            var Q122;
            Q122=makeQuery(id+"F1.opExtrude","SWEPT_EDGE",EDGE,{"disambiguationData":[OSD([sQuery(id+"F0.wireOp",EDGE,"E6.3.13.0"),sQuery(id+"F0.wireOp",EDGE,"E6.6.13.0")])]});
            var Q123;
            Q123=makeQuery(id+"F1.opExtrude","CAP_EDGE",EDGE,{"disambiguationData":[OSD([sQuery(id+"F0.wireOp",EDGE,"E5.1.1")])],"isStart":true});
            var Q124;
            Q124=makeQuery(id+"F1.opExtrude","CAP_EDGE",EDGE,{"disambiguationData":[OSD([sQuery(id+"F0.wireOp",EDGE,"E6.6.13.0")])],"isStart":true});
            var Q125;
            Q125=makeQuery(id+"F1.opExtrude","SWEPT_EDGE",EDGE,{"disambiguationData":[OSD([sQuery(id+"F0.wireOp",EDGE,"E6.3.12.0"),sQuery(id+"F0.wireOp",EDGE,"E6.6.12.0")])]});
            var Q126;
            Q126=makeQuery(id+"F1.opExtrude","CAP_EDGE",EDGE,{"disambiguationData":[OSD([sQuery(id+"F0.wireOp",EDGE,"E6.3.12.0")])],"isStart":false});
            var Q127;
            Q127=makeQuery(id+"F1.opExtrude","SWEPT_EDGE",EDGE,{"disambiguationData":[OSD([sQuery(id+"F0.wireOp",EDGE,"E6.2.10.0"),sQuery(id+"F0.wireOp",EDGE,"E6.3.10.0")])]});
            var Q128;
            Q128=makeQuery(id+"F1.opExtrude","CAP_EDGE",EDGE,{"disambiguationData":[OSD([sQuery(id+"F0.wireOp",EDGE,"E6.9.3.0")])],"isStart":false});
            var Q129;
            Q129=makeQuery(id+"F1.opExtrude","CAP_EDGE",EDGE,{"disambiguationData":[OSD([sQuery(id+"F0.wireOp",EDGE,"E6.6.7.0")])],"isStart":false});
            var Q130;
            Q130=makeQuery(id+"F1.opExtrude","CAP_EDGE",EDGE,{"disambiguationData":[OSD([sQuery(id+"F0.wireOp",EDGE,"E6.3.18.0")])],"isStart":true});
            var Q131;
            Q131=makeQuery(id+"F1.opExtrude","CAP_EDGE",EDGE,{"disambiguationData":[OSD([sQuery(id+"F0.wireOp",EDGE,"E6.9.16.0")])],"isStart":false});
            var Q132;
            Q132=makeQuery(id+"F1.opExtrude","SWEPT_EDGE",EDGE,{"disambiguationData":[OSD([sQuery(id+"F0.wireOp",EDGE,"E6.6.8.0"),sQuery(id+"F0.wireOp",EDGE,"E6.9.8.0")])]});
            var Q133;
            Q133=makeQuery(id+"F1.opExtrude","SWEPT_EDGE",EDGE,{"disambiguationData":[OSD([sQuery(id+"F0.wireOp",EDGE,"E6.6.9.0"),sQuery(id+"F0.wireOp",EDGE,"E6.9.9.0")])]});
            var Q134;
            Q134=makeQuery(id+"F1.opExtrude","CAP_EDGE",EDGE,{"disambiguationData":[OSD([sQuery(id+"F0.wireOp",EDGE,"E6.2.19.0")])],"isStart":false});
            var Q135;
            Q135=makeQuery(id+"F1.opExtrude","CAP_EDGE",EDGE,{"disambiguationData":[OSD([sQuery(id+"F0.wireOp",EDGE,"E6.6.8.0")])],"isStart":true});
            var Q136;
            Q136=makeQuery(id+"F1.opExtrude","SWEPT_EDGE",EDGE,{"disambiguationData":[OSD([sQuery(id+"F0.wireOp",EDGE,"E0"),sQuery(id+"F0.wireOp",EDGE,"E3")])]});
            var Q137;
            Q137=makeQuery(id+"F1.opExtrude","CAP_EDGE",EDGE,{"disambiguationData":[OSD([sQuery(id+"F0.wireOp",EDGE,"E6.3.3.0")])],"isStart":false});
            var Q138;
            Q138=makeQuery(id+"F1.opExtrude","CAP_EDGE",EDGE,{"disambiguationData":[OSD([sQuery(id+"F0.wireOp",EDGE,"E6.6.15.0")])],"isStart":false});
            var Q139;
            Q139=makeQuery(id+"F1.opExtrude","CAP_EDGE",EDGE,{"disambiguationData":[OSD([sQuery(id+"F0.wireOp",EDGE,"E3")])],"isStart":true});
            var Q140;
            Q140=makeQuery(id+"F1.opExtrude","CAP_EDGE",EDGE,{"disambiguationData":[OSD([sQuery(id+"F0.wireOp",EDGE,"E6.6.9.0")])],"isStart":true});
            var Q141;
            Q141=makeQuery(id+"F1.opExtrude","CAP_EDGE",EDGE,{"disambiguationData":[OSD([sQuery(id+"F0.wireOp",EDGE,"E6.9.18.0")])],"isStart":true});
            var Q142;
            Q142=makeQuery(id+"F1.opExtrude","SWEPT_EDGE",EDGE,{"disambiguationData":[OSD([sQuery(id+"F0.wireOp",EDGE,"E6.2.6.0"),sQuery(id+"F0.wireOp",EDGE,"E6.9.7.0")])]});
            var Q143;
            Q143=makeQuery(id+"F1.opExtrude","SWEPT_FACE",FACE,{"disambiguationData":[OSD([sQuery(id+"F0.wireOp",EDGE,"E6.3.18.0")])]});
            var Q144;
            Q144=makeQuery(id+"F1.opExtrude","SWEPT_EDGE",EDGE,{"disambiguationData":[OSD([sQuery(id+"F0.wireOp",EDGE,"E6.2.5.0"),sQuery(id+"F0.wireOp",EDGE,"E6.3.5.0")])]});
            var Q145;
            Q145=makeQuery(id+"F1.opExtrude","CAP_EDGE",EDGE,{"disambiguationData":[OSD([sQuery(id+"F0.wireOp",EDGE,"E6.3.10.0")])],"isStart":true});
            var Q146;
            Q146=makeQuery(id+"F1.opExtrude","CAP_EDGE",EDGE,{"disambiguationData":[OSD([sQuery(id+"F0.wireOp",EDGE,"E6.9.6.0")])],"isStart":false});
            var Q147;
            Q147=makeQuery(id+"F1.opExtrude","CAP_EDGE",EDGE,{"disambiguationData":[OSD([sQuery(id+"F0.wireOp",EDGE,"E6.9.16.0")])],"isStart":true});
            var Q148;
            Q148=makeQuery(id+"F1.opExtrude","CAP_EDGE",EDGE,{"disambiguationData":[OSD([sQuery(id+"F0.wireOp",EDGE,"E6.6.8.0")])],"isStart":false});
            var Q149;
            Q149=makeQuery(id+"F1.opExtrude","CAP_EDGE",EDGE,{"disambiguationData":[OSD([sQuery(id+"F0.wireOp",EDGE,"E6.2.14.0")])],"isStart":true});
            var Q150;
            Q150=makeQuery(id+"F1.opExtrude","SWEPT_EDGE",EDGE,{"disambiguationData":[OSD([sQuery(id+"F0.wireOp",EDGE,"E5.1.1"),sQuery(id+"F0.wireOp",EDGE,"E5.1.2")])]});
            var Q151;
            Q151=makeQuery(id+"F1.opExtrude","CAP_EDGE",EDGE,{"disambiguationData":[OSD([sQuery(id+"F0.wireOp",EDGE,"E6.6.10.0")])],"isStart":false});
            var Q152;
            Q152=makeQuery(id+"F1.opExtrude","CAP_EDGE",EDGE,{"disambiguationData":[OSD([sQuery(id+"F0.wireOp",EDGE,"E6.9.10.0")])],"isStart":false});
            var Q153;
            Q153=makeQuery(id+"F1.opExtrude","SWEPT_EDGE",EDGE,{"disambiguationData":[OSD([sQuery(id+"F0.wireOp",EDGE,"E6.6.3.0"),sQuery(id+"F0.wireOp",EDGE,"E6.9.3.0")])]});
            var Q154;
            Q154=makeQuery(id+"F1.opExtrude","CAP_EDGE",EDGE,{"disambiguationData":[OSD([sQuery(id+"F0.wireOp",EDGE,"E6.3.10.0")])],"isStart":false});
            var Q155;
            Q155=makeQuery(id+"F1.opExtrude","CAP_EDGE",EDGE,{"disambiguationData":[OSD([sQuery(id+"F0.wireOp",EDGE,"E6.2.10.0")])],"isStart":true});
            var Q156;
            Q156=makeQuery(id+"F1.opExtrude","CAP_EDGE",EDGE,{"disambiguationData":[OSD([sQuery(id+"F0.wireOp",EDGE,"E6.9.6.0")])],"isStart":true});
            var Q157;
            Q157=makeQuery(id+"F1.opExtrude","CAP_EDGE",EDGE,{"disambiguationData":[OSD([sQuery(id+"F0.wireOp",EDGE,"E6.6.6.0")])],"isStart":false});
            var Q158;
            Q158=makeQuery(id+"F1.opExtrude","CAP_EDGE",EDGE,{"disambiguationData":[OSD([sQuery(id+"F0.wireOp",EDGE,"E6.3.3.0")])],"isStart":true});
            var Q159;
            Q159=makeQuery(id+"F1.opExtrude","SWEPT_EDGE",EDGE,{"disambiguationData":[OSD([sQuery(id+"F0.wireOp",EDGE,"E6.2.4.0"),sQuery(id+"F0.wireOp",EDGE,"E6.9.5.0")])]});
            var Q160;
            Q160=makeQuery(id+"F1.opExtrude","CAP_EDGE",EDGE,{"disambiguationData":[OSD([sQuery(id+"F0.wireOp",EDGE,"E6.6.4.0")])],"isStart":false});
            var Q161;
            Q161=makeQuery(id+"F1.opExtrude","CAP_EDGE",EDGE,{"disambiguationData":[OSD([sQuery(id+"F0.wireOp",EDGE,"E6.6.4.0")])],"isStart":true});
            var Q162;
            Q162=makeQuery(id+"F1.opExtrude","CAP_EDGE",EDGE,{"disambiguationData":[OSD([sQuery(id+"F0.wireOp",EDGE,"E6.9.4.0")])],"isStart":false});
            var Q163;
            Q163=makeQuery(id+"F1.opExtrude","CAP_EDGE",EDGE,{"disambiguationData":[OSD([sQuery(id+"F0.wireOp",EDGE,"E6.9.15.0")])],"isStart":true});
            var Q164;
            Q164=makeQuery(id+"F1.opExtrude","CAP_EDGE",EDGE,{"disambiguationData":[OSD([sQuery(id+"F0.wireOp",EDGE,"E6.2.13.0")])],"isStart":false});
            var Q165;
            Q165=makeQuery(id+"F1.opExtrude","SWEPT_EDGE",EDGE,{"disambiguationData":[OSD([sQuery(id+"F0.wireOp",EDGE,"E6.2.8.0"),sQuery(id+"F0.wireOp",EDGE,"E6.9.9.0")])]});
            var Q166;
            Q166=makeQuery(id+"F1.opExtrude","SWEPT_EDGE",EDGE,{"disambiguationData":[OSD([sQuery(id+"F0.wireOp",EDGE,"E6.2.15.0"),sQuery(id+"F0.wireOp",EDGE,"E6.9.16.0")])]});
            var Q167;
            Q167=makeQuery(id+"F1.opExtrude","CAP_EDGE",EDGE,{"disambiguationData":[OSD([sQuery(id+"F0.wireOp",EDGE,"E5.2.2")])],"isStart":false});
            var Q168;
            Q168=makeQuery(id+"F1.opExtrude","SWEPT_EDGE",EDGE,{"disambiguationData":[OSD([sQuery(id+"F0.wireOp",EDGE,"E6.3.4.0"),sQuery(id+"F0.wireOp",EDGE,"E6.6.4.0")])]});
            var Q169;
            Q169=makeQuery(id+"F1.opExtrude","CAP_EDGE",EDGE,{"disambiguationData":[OSD([sQuery(id+"F0.wireOp",EDGE,"E6.6.19.0")])],"isStart":true});
            var Q170;
            Q170=makeQuery(id+"F1.opExtrude","CAP_EDGE",EDGE,{"disambiguationData":[OSD([sQuery(id+"F0.wireOp",EDGE,"E5.2.3")])],"isStart":true});
            var Q171;
            Q171=makeQuery(id+"F1.opExtrude","CAP_EDGE",EDGE,{"disambiguationData":[OSD([sQuery(id+"F0.wireOp",EDGE,"E6.2.7.0")])],"isStart":true});
            var Q172;
            Q172=makeQuery(id+"F1.opExtrude","CAP_EDGE",EDGE,{"disambiguationData":[OSD([sQuery(id+"F0.wireOp",EDGE,"E6.6.5.0")])],"isStart":false});
            var Q173;
            Q173=makeQuery(id+"F1.opExtrude","CAP_EDGE",EDGE,{"disambiguationData":[OSD([sQuery(id+"F0.wireOp",EDGE,"E6.3.8.0")])],"isStart":true});
            var Q174;
            Q174=makeQuery(id+"F1.opExtrude","CAP_EDGE",EDGE,{"disambiguationData":[OSD([sQuery(id+"F0.wireOp",EDGE,"E6.2.15.0")])],"isStart":true});
            var Q175;
            Q175=makeQuery(id+"F1.opExtrude","CAP_EDGE",EDGE,{"disambiguationData":[OSD([sQuery(id+"F0.wireOp",EDGE,"E6.2.13.0")])],"isStart":true});
            var Q176;
            Q176=makeQuery(id+"F1.opExtrude","CAP_EDGE",EDGE,{"disambiguationData":[OSD([sQuery(id+"F0.wireOp",EDGE,"E6.6.18.0")])],"isStart":true});
            var Q177;
            Q177=makeQuery(id+"F1.opExtrude","SWEPT_FACE",FACE,{"disambiguationData":[OSD([sQuery(id+"F0.wireOp",EDGE,"E6.3.11.0")])]});
            var Q178;
            Q178=makeQuery(id+"F1.opExtrude","CAP_EDGE",EDGE,{"disambiguationData":[OSD([sQuery(id+"F0.wireOp",EDGE,"E6.3.16.0")])],"isStart":true});
            var Q179;
            Q179=makeQuery(id+"F1.opExtrude","CAP_EDGE",EDGE,{"disambiguationData":[OSD([sQuery(id+"F0.wireOp",EDGE,"E6.3.19.0")])],"isStart":true});
            var Q180;
            Q180=makeQuery(id+"F1.opExtrude","SWEPT_EDGE",EDGE,{"disambiguationData":[OSD([sQuery(id+"F0.wireOp",EDGE,"E6.3.17.0"),sQuery(id+"F0.wireOp",EDGE,"E6.6.17.0")])]});
            var Q181;
            Q181=makeQuery(id+"F1.opExtrude","CAP_EDGE",EDGE,{"disambiguationData":[OSD([sQuery(id+"F0.wireOp",EDGE,"E6.9.15.0")])],"isStart":false});
            var Q182;
            Q182=makeQuery(id+"F1.opExtrude","SWEPT_EDGE",EDGE,{"disambiguationData":[OSD([sQuery(id+"F0.wireOp",EDGE,"E5.1.0"),sQuery(id+"F0.wireOp",EDGE,"E5.2.3")])]});
            var Q183;
            Q183=makeQuery(id+"F1.opExtrude","CAP_EDGE",EDGE,{"disambiguationData":[OSD([sQuery(id+"F0.wireOp",EDGE,"E6.3.5.0")])],"isStart":true});
            var Q184;
            Q184=makeQuery(id+"F1.opExtrude","SWEPT_FACE",FACE,{"disambiguationData":[OSD([sQuery(id+"F0.wireOp",EDGE,"E1.MirrorCS")])]});
            var Q185;
            Q185=makeQuery(id+"F1.opExtrude","SWEPT_EDGE",EDGE,{"disambiguationData":[OSD([sQuery(id+"F0.wireOp",EDGE,"E6.2.19.0"),sQuery(id+"F0.wireOp",EDGE,"E6.3.19.0")])]});
            var Q186;
            Q186=makeQuery(id+"F1.opExtrude","SWEPT_EDGE",EDGE,{"disambiguationData":[OSD([sQuery(id+"F0.wireOp",EDGE,"E6.2.6.0"),sQuery(id+"F0.wireOp",EDGE,"E6.3.6.0")])]});
            var Q187;
            Q187=makeQuery(id+"F1.opExtrude","CAP_EDGE",EDGE,{"disambiguationData":[OSD([sQuery(id+"F0.wireOp",EDGE,"E6.2.17.0")])],"isStart":false});
            var Q188;
            Q188=makeQuery(id+"F1.opExtrude","CAP_EDGE",EDGE,{"disambiguationData":[OSD([sQuery(id+"F0.wireOp",EDGE,"E6.6.12.0")])],"isStart":false});
            var Q189;
            Q189=makeQuery(id+"F1.opExtrude","CAP_EDGE",EDGE,{"disambiguationData":[OSD([sQuery(id+"F0.wireOp",EDGE,"E5.2.1")])],"isStart":true});
            var Q190;
            Q190=makeQuery(id+"F1.opExtrude","SWEPT_EDGE",EDGE,{"disambiguationData":[OSD([sQuery(id+"F0.wireOp",EDGE,"E6.3.11.0"),sQuery(id+"F0.wireOp",EDGE,"E6.6.11.0")])]});
            var Q191;
            Q191=makeQuery(id+"F1.opExtrude","CAP_EDGE",EDGE,{"disambiguationData":[OSD([sQuery(id+"F0.wireOp",EDGE,"E6.2.9.0")])],"isStart":false});
            var Q192;
            Q192=makeQuery(id+"F1.opExtrude","SWEPT_EDGE",EDGE,{"disambiguationData":[OSD([sQuery(id+"F0.wireOp",EDGE,"E6.2.16.0"),sQuery(id+"F0.wireOp",EDGE,"E6.3.16.0")])]});
            var Q193;
            Q193=makeQuery(id+"F1.opExtrude","CAP_EDGE",EDGE,{"disambiguationData":[OSD([sQuery(id+"F0.wireOp",EDGE,"E5.1.2")])],"isStart":true});
            var Q194;
            Q194=makeQuery(id+"F1.opExtrude","SWEPT_EDGE",EDGE,{"disambiguationData":[OSD([sQuery(id+"F0.wireOp",EDGE,"E6.3.9.0"),sQuery(id+"F0.wireOp",EDGE,"E6.6.9.0")])]});
            var Q195;
            Q195=makeQuery(id+"F1.opExtrude","CAP_EDGE",EDGE,{"disambiguationData":[OSD([sQuery(id+"F0.wireOp",EDGE,"E6.9.19.0")])],"isStart":false});
            var Q196;
            Q196=makeQuery(id+"F1.opExtrude","SWEPT_EDGE",EDGE,{"disambiguationData":[OSD([sQuery(id+"F0.wireOp",EDGE,"E6.2.11.0"),sQuery(id+"F0.wireOp",EDGE,"E6.3.11.0")])]});
            var Q197;
            Q197=makeQuery(id+"F1.opExtrude","CAP_EDGE",EDGE,{"disambiguationData":[OSD([sQuery(id+"F0.wireOp",EDGE,"E6.9.11.0")])],"isStart":true});
            var Q198;
            Q198=makeQuery(id+"F1.opExtrude","SWEPT_EDGE",EDGE,{"disambiguationData":[OSD([sQuery(id+"F0.wireOp",EDGE,"E6.2.8.0"),sQuery(id+"F0.wireOp",EDGE,"E6.3.8.0")])]});
            var Q199;
            Q199=makeQuery(id+"F1.opExtrude","CAP_EDGE",EDGE,{"disambiguationData":[OSD([sQuery(id+"F0.wireOp",EDGE,"E6.6.16.0")])],"isStart":false});
            var Q200;
            Q200=makeQuery(id+"F1.opExtrude","SWEPT_EDGE",EDGE,{"disambiguationData":[OSD([sQuery(id+"F0.wireOp",EDGE,"E6.6.19.0"),sQuery(id+"F0.wireOp",EDGE,"E6.9.19.0")])]});
            var Q201;
            Q201=makeQuery(id+"F1.opExtrude","CAP_EDGE",EDGE,{"disambiguationData":[OSD([sQuery(id+"F0.wireOp",EDGE,"E6.6.9.0")])],"isStart":false});
            var Q202;
            Q202=makeQuery(id+"F1.opExtrude","SWEPT_EDGE",EDGE,{"disambiguationData":[OSD([sQuery(id+"F0.wireOp",EDGE,"E6.6.14.0"),sQuery(id+"F0.wireOp",EDGE,"E6.9.14.0")])]});
            var Q203;
            Q203=makeQuery(id+"F1.opExtrude","SWEPT_EDGE",EDGE,{"disambiguationData":[OSD([sQuery(id+"F0.wireOp",EDGE,"E6.3.19.0"),sQuery(id+"F0.wireOp",EDGE,"E6.6.19.0")])]});
            var Q204;
            Q204=makeQuery(id+"F1.opExtrude","CAP_EDGE",EDGE,{"disambiguationData":[OSD([sQuery(id+"F0.wireOp",EDGE,"E6.2.5.0")])],"isStart":false});
            var Q205;
            Q205=makeQuery(id+"F1.opExtrude","CAP_EDGE",EDGE,{"disambiguationData":[OSD([sQuery(id+"F0.wireOp",EDGE,"E6.6.17.0")])],"isStart":true});
            var Q206;
            Q206=makeQuery(id+"F1.opExtrude","CAP_EDGE",EDGE,{"disambiguationData":[OSD([sQuery(id+"F0.wireOp",EDGE,"E6.2.12.0")])],"isStart":true});
            var Q207;
            Q207=makeQuery(id+"F1.opExtrude","CAP_EDGE",EDGE,{"disambiguationData":[OSD([sQuery(id+"F0.wireOp",EDGE,"E6.2.9.0")])],"isStart":true});
            var Q208;
            Q208=makeQuery(id+"F1.opExtrude","SWEPT_EDGE",EDGE,{"disambiguationData":[OSD([sQuery(id+"F0.wireOp",EDGE,"E6.6.13.0"),sQuery(id+"F0.wireOp",EDGE,"E6.9.13.0")])]});
            var Q209;
            Q209=makeQuery(id+"F1.opExtrude","CAP_EDGE",EDGE,{"disambiguationData":[OSD([sQuery(id+"F0.wireOp",EDGE,"E6.2.5.0")])],"isStart":true});
            var Q210;
            Q210=makeQuery(id+"F1.opExtrude","CAP_EDGE",EDGE,{"disambiguationData":[OSD([sQuery(id+"F0.wireOp",EDGE,"E6.3.16.0")])],"isStart":false});
            var Q211;
            Q211=makeQuery(id+"F1.opExtrude","CAP_EDGE",EDGE,{"disambiguationData":[OSD([sQuery(id+"F0.wireOp",EDGE,"E6.9.11.0")])],"isStart":false});
            var Q212;
            Q212=makeQuery(id+"F1.opExtrude","CAP_EDGE",EDGE,{"disambiguationData":[OSD([sQuery(id+"F0.wireOp",EDGE,"E6.3.4.0")])],"isStart":false});
            var Q213;
            Q213=makeQuery(id+"F1.opExtrude","CAP_EDGE",EDGE,{"disambiguationData":[OSD([sQuery(id+"F0.wireOp",EDGE,"E6.9.4.0")])],"isStart":true});
            var Q214;
            Q214=makeQuery(id+"F1.opExtrude","CAP_EDGE",EDGE,{"disambiguationData":[OSD([sQuery(id+"F0.wireOp",EDGE,"E6.9.8.0")])],"isStart":false});
            var Q215;
            Q215=makeQuery(id+"F1.opExtrude","SWEPT_EDGE",EDGE,{"disambiguationData":[OSD([sQuery(id+"F0.wireOp",EDGE,"E1.MirrorCS"),sQuery(id+"F0.wireOp",EDGE,"E5.1.3")])]});
            var Q216;
            Q216=makeQuery(id+"F1.opExtrude","CAP_EDGE",EDGE,{"disambiguationData":[OSD([sQuery(id+"F0.wireOp",EDGE,"E6.6.15.0")])],"isStart":true});
            var Q217;
            Q217=makeQuery(id+"F1.opExtrude","SWEPT_EDGE",EDGE,{"disambiguationData":[OSD([sQuery(id+"F0.wireOp",EDGE,"E6.6.11.0"),sQuery(id+"F0.wireOp",EDGE,"E6.9.11.0")])]});
            var Q218;
            Q218=makeQuery(id+"F1.opExtrude","SWEPT_EDGE",EDGE,{"disambiguationData":[OSD([sQuery(id+"F0.wireOp",EDGE,"E1.MirrorCS"),sQuery(id+"F0.wireOp",EDGE,"E3")])]});
            var Q219;
            Q219=makeQuery(id+"F1.opExtrude","CAP_EDGE",EDGE,{"disambiguationData":[OSD([sQuery(id+"F0.wireOp",EDGE,"E6.2.16.0")])],"isStart":false});
            var Q220;
            Q220=makeQuery(id+"F1.opExtrude","SWEPT_EDGE",EDGE,{"disambiguationData":[OSD([sQuery(id+"F0.wireOp",EDGE,"E6.6.18.0"),sQuery(id+"F0.wireOp",EDGE,"E6.9.18.0")])]});
            var Q221;
            Q221=makeQuery(id+"F1.opExtrude","CAP_EDGE",EDGE,{"disambiguationData":[OSD([sQuery(id+"F0.wireOp",EDGE,"E6.9.3.0")])],"isStart":true});
            var Q222;
            Q222=makeQuery(id+"F1.opExtrude","SWEPT_FACE",FACE,{"disambiguationData":[OSD([sQuery(id+"F0.wireOp",EDGE,"E6.6.3.0")])]});
            var Q223;
            Q223=makeQuery(id+"F1.opExtrude","CAP_EDGE",EDGE,{"disambiguationData":[OSD([sQuery(id+"F0.wireOp",EDGE,"E6.2.19.0")])],"isStart":true});
            var Q224;
            Q224=makeQuery(id+"F1.opExtrude","SWEPT_EDGE",EDGE,{"disambiguationData":[OSD([sQuery(id+"F0.wireOp",EDGE,"E6.2.12.0"),sQuery(id+"F0.wireOp",EDGE,"E6.9.13.0")])]});
            var Q225;
            Q225=makeQuery(id+"F1.opExtrude","CAP_EDGE",EDGE,{"disambiguationData":[OSD([sQuery(id+"F0.wireOp",EDGE,"E6.3.19.0")])],"isStart":false});
            var Q226;
            Q226=makeQuery(id+"F1.opExtrude","CAP_EDGE",EDGE,{"disambiguationData":[OSD([sQuery(id+"F0.wireOp",EDGE,"E6.9.10.0")])],"isStart":true});
            var Q227;
            Q227=makeQuery(id+"F1.opExtrude","CAP_EDGE",EDGE,{"disambiguationData":[OSD([sQuery(id+"F0.wireOp",EDGE,"E6.6.13.0")])],"isStart":false});
            var Q228;
            Q228=makeQuery(id+"F1.opExtrude","SWEPT_EDGE",EDGE,{"disambiguationData":[OSD([sQuery(id+"F0.wireOp",EDGE,"E6.2.7.0"),sQuery(id+"F0.wireOp",EDGE,"E6.3.7.0")])]});
            var Q229;
            Q229=makeQuery(id+"F1.opExtrude","SWEPT_EDGE",EDGE,{"disambiguationData":[OSD([sQuery(id+"F0.wireOp",EDGE,"E6.6.7.0"),sQuery(id+"F0.wireOp",EDGE,"E6.9.7.0")])]});
            var Q230;
            Q230=makeQuery(id+"F1.opExtrude","CAP_EDGE",EDGE,{"disambiguationData":[OSD([sQuery(id+"F0.wireOp",EDGE,"E6.9.14.0")])],"isStart":false});
            var Q231;
            Q231=makeQuery(id+"F1.opExtrude","SWEPT_FACE",FACE,{"disambiguationData":[OSD([sQuery(id+"F0.wireOp",EDGE,"E0")])]});
            var Q232;
            Q232=makeQuery(id+"F1.opExtrude","CAP_EDGE",EDGE,{"disambiguationData":[OSD([sQuery(id+"F0.wireOp",EDGE,"E6.2.7.0")])],"isStart":false});
            var Q233;
            Q233=makeQuery(id+"F1.opExtrude","CAP_EDGE",EDGE,{"disambiguationData":[OSD([sQuery(id+"F0.wireOp",EDGE,"E6.9.9.0")])],"isStart":false});
            var Q234;
            Q234=makeQuery(id+"F1.opExtrude","CAP_EDGE",EDGE,{"disambiguationData":[OSD([sQuery(id+"F0.wireOp",EDGE,"E6.2.3.0")])],"isStart":false});
            var Q235;
            Q235=makeQuery(id+"F1.opExtrude","CAP_EDGE",EDGE,{"disambiguationData":[OSD([sQuery(id+"F0.wireOp",EDGE,"E5.1.0")])],"isStart":false});
            var Q236;
            Q236=makeQuery(id+"F1.opExtrude","CAP_EDGE",EDGE,{"disambiguationData":[OSD([sQuery(id+"F0.wireOp",EDGE,"E5.2.2")])],"isStart":true});
            var Q237;
            Q237=makeQuery(id+"F1.opExtrude","SWEPT_EDGE",EDGE,{"disambiguationData":[OSD([sQuery(id+"F0.wireOp",EDGE,"E6.2.3.0"),sQuery(id+"F0.wireOp",EDGE,"E6.9.4.0")])]});
            var Q238;
            Q238=makeQuery(id+"F1.opExtrude","SWEPT_EDGE",EDGE,{"disambiguationData":[OSD([sQuery(id+"F0.wireOp",EDGE,"E5.2.2"),sQuery(id+"F0.wireOp",EDGE,"E5.2.3")])]});
            var Q239;
            Q239=makeQuery(id+"F1.opExtrude","SWEPT_EDGE",EDGE,{"disambiguationData":[OSD([sQuery(id+"F0.wireOp",EDGE,"E6.2.18.0"),sQuery(id+"F0.wireOp",EDGE,"E6.3.18.0")])]});
            var Q240;
            Q240=makeQuery(id+"F1.opExtrude","SWEPT_FACE",FACE,{"disambiguationData":[OSD([sQuery(id+"F0.wireOp",EDGE,"E2")])]});
            var Q241;
            Q241=makeQuery(id+"F1.opExtrude","CAP_EDGE",EDGE,{"disambiguationData":[OSD([sQuery(id+"F0.wireOp",EDGE,"E6.9.8.0")])],"isStart":true});
            var Q242;
            Q242=makeQuery(id+"F1.opExtrude","CAP_EDGE",EDGE,{"disambiguationData":[OSD([sQuery(id+"F0.wireOp",EDGE,"E6.3.8.0")])],"isStart":false});
            var Q243;
            Q243=makeQuery(id+"F1.opExtrude","CAP_EDGE",EDGE,{"disambiguationData":[OSD([sQuery(id+"F0.wireOp",EDGE,"E6.3.14.0")])],"isStart":true});
            var Q244;
            Q244=makeQuery(id+"F1.opExtrude","SWEPT_EDGE",EDGE,{"disambiguationData":[OSD([sQuery(id+"F0.wireOp",EDGE,"E6.2.9.0"),sQuery(id+"F0.wireOp",EDGE,"E6.9.10.0")])]});
            var Q245;
            Q245=makeQuery(id+"F1.opExtrude","CAP_EDGE",EDGE,{"disambiguationData":[OSD([sQuery(id+"F0.wireOp",EDGE,"E6.2.4.0")])],"isStart":false});
            var Q246;
            Q246=makeQuery(id+"F1.opExtrude","SWEPT_EDGE",EDGE,{"disambiguationData":[OSD([sQuery(id+"F0.wireOp",EDGE,"E6.6.17.0"),sQuery(id+"F0.wireOp",EDGE,"E6.9.17.0")])]});
            var Q247;
            Q247=makeQuery(id+"F1.opExtrude","CAP_EDGE",EDGE,{"disambiguationData":[OSD([sQuery(id+"F0.wireOp",EDGE,"E6.2.11.0")])],"isStart":false});
            var Q248;
            Q248=makeQuery(id+"F1.opExtrude","CAP_EDGE",EDGE,{"disambiguationData":[OSD([sQuery(id+"F0.wireOp",EDGE,"E6.2.3.0")])],"isStart":true});
            var Q249;
            Q249=makeQuery(id+"F1.opExtrude","SWEPT_EDGE",EDGE,{"disambiguationData":[OSD([sQuery(id+"F0.wireOp",EDGE,"E5.2.1"),sQuery(id+"F0.wireOp",EDGE,"E5.2.2")])]});
            var Q250;
            Q250=makeQuery(id+"F1.opExtrude","CAP_EDGE",EDGE,{"disambiguationData":[OSD([sQuery(id+"F0.wireOp",EDGE,"E6.9.12.0")])],"isStart":false});
            var Q251;
            Q251=makeQuery(id+"F1.opExtrude","CAP_EDGE",EDGE,{"disambiguationData":[OSD([sQuery(id+"F0.wireOp",EDGE,"E6.6.5.0")])],"isStart":true});
            var Q252;
            Q252=makeQuery(id+"F1.opExtrude","CAP_EDGE",EDGE,{"disambiguationData":[OSD([sQuery(id+"F0.wireOp",EDGE,"E6.6.7.0")])],"isStart":true});
            var Q253;
            Q253=makeQuery(id+"F1.opExtrude","CAP_EDGE",EDGE,{"disambiguationData":[OSD([sQuery(id+"F0.wireOp",EDGE,"E6.9.7.0")])],"isStart":false});
            var Q254;
            Q254=makeQuery(id+"F1.opExtrude","SWEPT_EDGE",EDGE,{"disambiguationData":[OSD([sQuery(id+"F0.wireOp",EDGE,"E6.2.14.0"),sQuery(id+"F0.wireOp",EDGE,"E6.3.14.0")])]});
            var Q255;
            Q255=makeQuery(id+"F1.opExtrude","CAP_EDGE",EDGE,{"disambiguationData":[OSD([sQuery(id+"F0.wireOp",EDGE,"E6.6.14.0")])],"isStart":false});
            var Q256;
            Q256=makeQuery(id+"F1.opExtrude","CAP_EDGE",EDGE,{"disambiguationData":[OSD([sQuery(id+"F0.wireOp",EDGE,"E6.2.6.0")])],"isStart":false});
            var Q257;
            Q257=makeQuery(id+"F1.opExtrude","CAP_EDGE",EDGE,{"disambiguationData":[OSD([sQuery(id+"F0.wireOp",EDGE,"E6.3.13.0")])],"isStart":false});
            var Q258;
            Q258=makeQuery(id+"F1.opExtrude","SWEPT_EDGE",EDGE,{"disambiguationData":[OSD([sQuery(id+"F0.wireOp",EDGE,"E5.2.0"),sQuery(id+"F0.wireOp",EDGE,"E6.9.3.0")])]});
            var Q259;
            Q259=makeQuery(id+"F1.opExtrude","SWEPT_FACE",FACE,{"disambiguationData":[OSD([sQuery(id+"F0.wireOp",EDGE,"E6.2.8.0")])]});
            var Q260;
            Q260=makeQuery(id+"F1.opExtrude","SWEPT_EDGE",EDGE,{"disambiguationData":[OSD([sQuery(id+"F0.wireOp",EDGE,"E6.6.10.0"),sQuery(id+"F0.wireOp",EDGE,"E6.9.10.0")])]});
            var Q261;
            Q261=makeQuery(id+"F1.opExtrude","SWEPT_EDGE",EDGE,{"disambiguationData":[OSD([sQuery(id+"F0.wireOp",EDGE,"E6.3.18.0"),sQuery(id+"F0.wireOp",EDGE,"E6.6.18.0")])]});
            var Q262;
            Q262=makeQuery(id+"F1.opExtrude","SWEPT_FACE",FACE,{"disambiguationData":[OSD([sQuery(id+"F0.wireOp",EDGE,"E6.3.12.0")])]});
            var Q263;
            Q263=makeQuery(id+"F1.opExtrude","CAP_EDGE",EDGE,{"disambiguationData":[OSD([sQuery(id+"F0.wireOp",EDGE,"E6.6.17.0")])],"isStart":false});
            var Q264;
            Q264=makeQuery(id+"F1.opExtrude","SWEPT_EDGE",EDGE,{"disambiguationData":[OSD([sQuery(id+"F0.wireOp",EDGE,"E2"),sQuery(id+"F0.wireOp",EDGE,"E6.2.19.0")])]});
            var Q265;
            Q265=makeQuery(id+"F1.opExtrude","SWEPT_EDGE",EDGE,{"disambiguationData":[OSD([sQuery(id+"F0.wireOp",EDGE,"E6.6.6.0"),sQuery(id+"F0.wireOp",EDGE,"E6.9.6.0")])]});
            var Q266;
            Q266=makeQuery(id+"F1.opExtrude","SWEPT_EDGE",EDGE,{"disambiguationData":[OSD([sQuery(id+"F0.wireOp",EDGE,"E6.3.14.0"),sQuery(id+"F0.wireOp",EDGE,"E6.6.14.0")])]});
            var Q267;
            Q267=makeQuery(id+"F1.opExtrude","SWEPT_FACE",FACE,{"disambiguationData":[OSD([sQuery(id+"F0.wireOp",EDGE,"E6.6.14.0")])]});
            var Q268;
            Q268=makeQuery(id+"F1.opExtrude","CAP_EDGE",EDGE,{"disambiguationData":[OSD([sQuery(id+"F0.wireOp",EDGE,"E6.9.5.0")])],"isStart":false});
            var Q269;
            Q269=makeQuery(id+"F1.opExtrude","CAP_EDGE",EDGE,{"disambiguationData":[OSD([sQuery(id+"F0.wireOp",EDGE,"E5.1.3")])],"isStart":true});
            var Q270;
            Q270=makeQuery(id+"F1.opExtrude","CAP_EDGE",EDGE,{"disambiguationData":[OSD([sQuery(id+"F0.wireOp",EDGE,"E6.2.4.0")])],"isStart":true});
            var Q271;
            Q271=makeQuery(id+"F1.opExtrude","SWEPT_EDGE",EDGE,{"disambiguationData":[OSD([sQuery(id+"F0.wireOp",EDGE,"E6.3.8.0"),sQuery(id+"F0.wireOp",EDGE,"E6.6.8.0")])]});
            var Q272;
            Q272=makeQuery(id+"F1.opExtrude","SWEPT_EDGE",EDGE,{"disambiguationData":[OSD([sQuery(id+"F0.wireOp",EDGE,"E6.6.4.0"),sQuery(id+"F0.wireOp",EDGE,"E6.9.4.0")])]});
            var Q273;
            Q273=makeQuery(id+"F1.opExtrude","CAP_EDGE",EDGE,{"disambiguationData":[OSD([sQuery(id+"F0.wireOp",EDGE,"E6.3.4.0")])],"isStart":true});
            var Q274;
            Q274=makeQuery(id+"F1.opExtrude","CAP_EDGE",EDGE,{"disambiguationData":[OSD([sQuery(id+"F0.wireOp",EDGE,"E5.1.0")])],"isStart":true});
            var Q275;
            Q275=makeQuery(id+"F1.opExtrude","CAP_EDGE",EDGE,{"disambiguationData":[OSD([sQuery(id+"F0.wireOp",EDGE,"E6.9.12.0")])],"isStart":true});
            var Q276;
            Q276=makeQuery(id+"F1.opExtrude","SWEPT_EDGE",EDGE,{"disambiguationData":[OSD([sQuery(id+"F0.wireOp",EDGE,"E6.2.17.0"),sQuery(id+"F0.wireOp",EDGE,"E6.3.17.0")])]});
            var Q277;
            Q277=makeQuery(id+"F1.opExtrude","CAP_EDGE",EDGE,{"disambiguationData":[OSD([sQuery(id+"F0.wireOp",EDGE,"E6.6.6.0")])],"isStart":true});
            var Q278;
            Q278=makeQuery(id+"F1.opExtrude","CAP_EDGE",EDGE,{"disambiguationData":[OSD([sQuery(id+"F0.wireOp",EDGE,"E6.3.6.0")])],"isStart":false});
            var Q279;
            Q279=makeQuery(id+"F1.opExtrude","CAP_EDGE",EDGE,{"disambiguationData":[OSD([sQuery(id+"F0.wireOp",EDGE,"E6.2.6.0")])],"isStart":true});
            var Q280;
            Q280=makeQuery(id+"F1.opExtrude","SWEPT_EDGE",EDGE,{"disambiguationData":[OSD([sQuery(id+"F0.wireOp",EDGE,"E6.2.14.0"),sQuery(id+"F0.wireOp",EDGE,"E6.9.15.0")])]});
            var Q281;
            Q281=makeQuery(id+"F1.opExtrude","CAP_EDGE",EDGE,{"disambiguationData":[OSD([sQuery(id+"F0.wireOp",EDGE,"E6.3.7.0")])],"isStart":true});
            var Q282;
            Q282=makeQuery(id+"F1.opExtrude","CAP_EDGE",EDGE,{"disambiguationData":[OSD([sQuery(id+"F0.wireOp",EDGE,"E6.2.15.0")])],"isStart":false});
            var Q283;
            Q283=makeQuery(id+"F1.opExtrude","SWEPT_EDGE",EDGE,{"disambiguationData":[OSD([sQuery(id+"F0.wireOp",EDGE,"E6.3.16.0"),sQuery(id+"F0.wireOp",EDGE,"E6.6.16.0")])]});
            var Q284;
            Q284=makeQuery(id+"F1.opExtrude","CAP_EDGE",EDGE,{"disambiguationData":[OSD([sQuery(id+"F0.wireOp",EDGE,"E6.3.5.0")])],"isStart":false});
            var Q285;
            Q285=makeQuery(id+"F1.opExtrude","CAP_EDGE",EDGE,{"disambiguationData":[OSD([sQuery(id+"F0.wireOp",EDGE,"E6.2.17.0")])],"isStart":true});
            var Q286;
            Q286=makeQuery(id+"F1.opExtrude","CAP_EDGE",EDGE,{"disambiguationData":[OSD([sQuery(id+"F0.wireOp",EDGE,"E6.2.16.0")])],"isStart":true});
            var Q287;
            Q287=makeQuery(id+"F1.opExtrude","CAP_EDGE",EDGE,{"disambiguationData":[OSD([sQuery(id+"F0.wireOp",EDGE,"E6.9.19.0")])],"isStart":true});
            var Q288;
            Q288=makeQuery(id+"F1.opExtrude","CAP_EDGE",EDGE,{"disambiguationData":[OSD([sQuery(id+"F0.wireOp",EDGE,"E6.9.14.0")])],"isStart":true});
            var Q289;
            Q289=makeQuery(id+"F1.opExtrude","CAP_EDGE",EDGE,{"disambiguationData":[OSD([sQuery(id+"F0.wireOp",EDGE,"E6.3.17.0")])],"isStart":false});
            var Q290;
            Q290=makeQuery(id+"F1.opExtrude","CAP_EDGE",EDGE,{"disambiguationData":[OSD([sQuery(id+"F0.wireOp",EDGE,"E6.3.15.0")])],"isStart":false});
            var Q291;
            Q291=makeQuery(id+"F1.opExtrude","CAP_EDGE",EDGE,{"disambiguationData":[OSD([sQuery(id+"F0.wireOp",EDGE,"E6.6.12.0")])],"isStart":true});
            var Q292;
            Q292=makeQuery(id+"F1.opExtrude","SWEPT_EDGE",EDGE,{"disambiguationData":[OSD([sQuery(id+"F0.wireOp",EDGE,"E5.1.2"),sQuery(id+"F0.wireOp",EDGE,"E5.1.3")])]});
            var Q293;
            Q293=makeQuery(id+"F1.opExtrude","CAP_EDGE",EDGE,{"disambiguationData":[OSD([sQuery(id+"F0.wireOp",EDGE,"E6.3.13.0")])],"isStart":true});
            var Q294;
            Q294=makeQuery(id+"F1.opExtrude","SWEPT_EDGE",EDGE,{"disambiguationData":[OSD([sQuery(id+"F0.wireOp",EDGE,"E6.2.3.0"),sQuery(id+"F0.wireOp",EDGE,"E6.3.3.0")])]});
            var Q295;
            Q295=makeQuery(id+"F1.opExtrude","CAP_EDGE",EDGE,{"disambiguationData":[OSD([sQuery(id+"F0.wireOp",EDGE,"E6.3.9.0")])],"isStart":true});
            var Q296;
            Q296=makeQuery(id+"F1.opExtrude","CAP_EDGE",EDGE,{"disambiguationData":[OSD([sQuery(id+"F0.wireOp",EDGE,"E6.6.3.0")])],"isStart":true});
            var Q297;
            Q297=makeQuery(id+"F1.opExtrude","CAP_EDGE",EDGE,{"disambiguationData":[OSD([sQuery(id+"F0.wireOp",EDGE,"E6.2.8.0")])],"isStart":false});
            var Q298;
            Q298=makeQuery(id+"F1.opExtrude","CAP_EDGE",EDGE,{"disambiguationData":[OSD([sQuery(id+"F0.wireOp",EDGE,"E5.2.3")])],"isStart":false});
            var Q299;
            Q299=makeQuery(id+"F1.opExtrude","SWEPT_EDGE",EDGE,{"disambiguationData":[OSD([sQuery(id+"F0.wireOp",EDGE,"E6.3.6.0"),sQuery(id+"F0.wireOp",EDGE,"E6.6.6.0")])]});
            var Q300;
            Q300=makeQuery(id+"F1.opExtrude","SWEPT_EDGE",EDGE,{"disambiguationData":[OSD([sQuery(id+"F0.wireOp",EDGE,"E6.2.10.0"),sQuery(id+"F0.wireOp",EDGE,"E6.9.11.0")])]});
            var Q301;
            Q301=makeQuery(id+"F1.opExtrude","CAP_EDGE",EDGE,{"disambiguationData":[OSD([sQuery(id+"F0.wireOp",EDGE,"E6.3.9.0")])],"isStart":false});
            var Q302;
            Q302=makeQuery(id+"F1.opExtrude","CAP_EDGE",EDGE,{"disambiguationData":[OSD([sQuery(id+"F0.wireOp",EDGE,"E1.MirrorCS")])],"isStart":true});
            var Q303;
            Q303=makeQuery(id+"F1.opExtrude","CAP_EDGE",EDGE,{"disambiguationData":[OSD([sQuery(id+"F0.wireOp",EDGE,"E5.1.3")])],"isStart":false});
            var Q304;
            Q304=makeQuery(id+"F1.opExtrude","CAP_EDGE",EDGE,{"disambiguationData":[OSD([sQuery(id+"F0.wireOp",EDGE,"E0")])],"isStart":false});
            var Q305;
            Q305=makeQuery(id+"F1.opExtrude","CAP_EDGE",EDGE,{"disambiguationData":[OSD([sQuery(id+"F0.wireOp",EDGE,"E6.3.11.0")])],"isStart":false});
            var Q306;
            Q306=makeQuery(id+"F1.opExtrude","CAP_EDGE",EDGE,{"disambiguationData":[OSD([sQuery(id+"F0.wireOp",EDGE,"E2")])],"isStart":true});
            var Q307;
            Q307=makeQuery(id+"F1.opExtrude","SWEPT_EDGE",EDGE,{"disambiguationData":[OSD([sQuery(id+"F0.wireOp",EDGE,"E6.2.11.0"),sQuery(id+"F0.wireOp",EDGE,"E6.9.12.0")])]});
            var Q308;
            Q308=makeQuery(id+"F1.opExtrude","SWEPT_EDGE",EDGE,{"disambiguationData":[OSD([sQuery(id+"F0.wireOp",EDGE,"E6.2.16.0"),sQuery(id+"F0.wireOp",EDGE,"E6.9.17.0")])]});
            var Q309;
            Q309=makeQuery(id+"F1.opExtrude","SWEPT_EDGE",EDGE,{"disambiguationData":[OSD([sQuery(id+"F0.wireOp",EDGE,"E6.2.4.0"),sQuery(id+"F0.wireOp",EDGE,"E6.3.4.0")])]});
            var Q310;
            Q310=makeQuery(id+"F1.opExtrude","SWEPT_EDGE",EDGE,{"disambiguationData":[OSD([sQuery(id+"F0.wireOp",EDGE,"E0"),sQuery(id+"F0.wireOp",EDGE,"E2")])]});
            var Q311;
            Q311=makeQuery(id+"F1.opExtrude","CAP_EDGE",EDGE,{"disambiguationData":[OSD([sQuery(id+"F0.wireOp",EDGE,"E5.1.1")])],"isStart":false});
            var Q312;
            Q312=makeQuery(id+"F1.opExtrude","CAP_EDGE",EDGE,{"disambiguationData":[OSD([sQuery(id+"F0.wireOp",EDGE,"E5.2.1")])],"isStart":false});
            var Q313;
            Q313=makeQuery(id+"F1.opExtrude","CAP_EDGE",EDGE,{"disambiguationData":[OSD([sQuery(id+"F0.wireOp",EDGE,"E3")])],"isStart":false});
            var Q314;
            Q314=makeQuery(id+"F1.opExtrude","SWEPT_EDGE",EDGE,{"disambiguationData":[OSD([sQuery(id+"F0.wireOp",EDGE,"E6.3.10.0"),sQuery(id+"F0.wireOp",EDGE,"E6.6.10.0")])]});
            var Q315;
            Q315=makeQuery(id+"F1.opExtrude","CAP_EDGE",EDGE,{"disambiguationData":[OSD([sQuery(id+"F0.wireOp",EDGE,"E2")])],"isStart":false});
            chamfer(context, id + "F2", {"entities" : qUnion([Q0, Q1, Q2, Q3, Q4, Q5, Q6, Q7, Q8, Q9, Q10, Q11, Q12, Q13, Q14, Q15, Q16, Q17, Q18, Q19, Q20, Q21, Q22, Q23, Q24, Q25, Q26, Q27, Q28, Q29, Q30, Q31, Q32, Q33, Q34, Q35, Q36, Q37, Q38, Q39, Q40, Q41, Q42, Q43, Q44, Q45, Q46, Q47, Q48, Q49, Q50, Q51, Q52, Q53, Q54, Q55, Q56, Q57, Q58, Q59, Q60, Q61, Q62, Q63, Q64, Q65, Q66, Q67, Q68, Q69, Q70, Q71, Q72, Q73, Q74, Q75, Q76, Q77, Q78, Q79, Q80, Q81, Q82, Q83, Q84, Q85, Q86, Q87, Q88, Q89, Q90, Q91, Q92, Q93, Q94, Q95, Q96, Q97, Q98, Q99, Q100, Q101, Q102, Q103, Q104, Q105, Q106, Q107, Q108, Q109, Q110, Q111, Q112, Q113, Q114, Q115, Q116, Q117, Q118, Q119, Q120, Q121, Q122, Q123, Q124, Q125, Q126, Q127, Q128, Q129, Q130, Q131, Q132, Q133, Q134, Q135, Q136, Q137, Q138, Q139, Q140, Q141, Q142, Q143, Q144, Q145, Q146, Q147, Q148, Q149, Q150, Q151, Q152, Q153, Q154, Q155, Q156, Q157, Q158, Q159, Q160, Q161, Q162, Q163, Q164, Q165, Q166, Q167, Q168, Q169, Q170, Q171, Q172, Q173, Q174, Q175, Q176, Q177, Q178, Q179, Q180, Q181, Q182, Q183, Q184, Q185, Q186, Q187, Q188, Q189, Q190, Q191, Q192, Q193, Q194, Q195, Q196, Q197, Q198, Q199, Q200, Q201, Q202, Q203, Q204, Q205, Q206, Q207, Q208, Q209, Q210, Q211, Q212, Q213, Q214, Q215, Q216, Q217, Q218, Q219, Q220, Q221, Q222, Q223, Q224, Q225, Q226, Q227, Q228, Q229, Q230, Q231, Q232, Q233, Q234, Q235, Q236, Q237, Q238, Q239, Q240, Q241, Q242, Q243, Q244, Q245, Q246, Q247, Q248, Q249, Q250, Q251, Q252, Q253, Q254, Q255, Q256, Q257, Q258, Q259, Q260, Q261, Q262, Q263, Q264, Q265, Q266, Q267, Q268, Q269, Q270, Q271, Q272, Q273, Q274, Q275, Q276, Q277, Q278, Q279, Q280, Q281, Q282, Q283, Q284, Q285, Q286, Q287, Q288, Q289, Q290, Q291, Q292, Q293, Q294, Q295, Q296, Q297, Q298, Q299, Q300, Q301, Q302, Q303, Q304, Q305, Q306, Q307, Q308, Q309, Q310, Q311, Q312, Q313, Q314, Q315]), "width" : .5 * mm, "tangentPropagation" : true});
        }
    });
